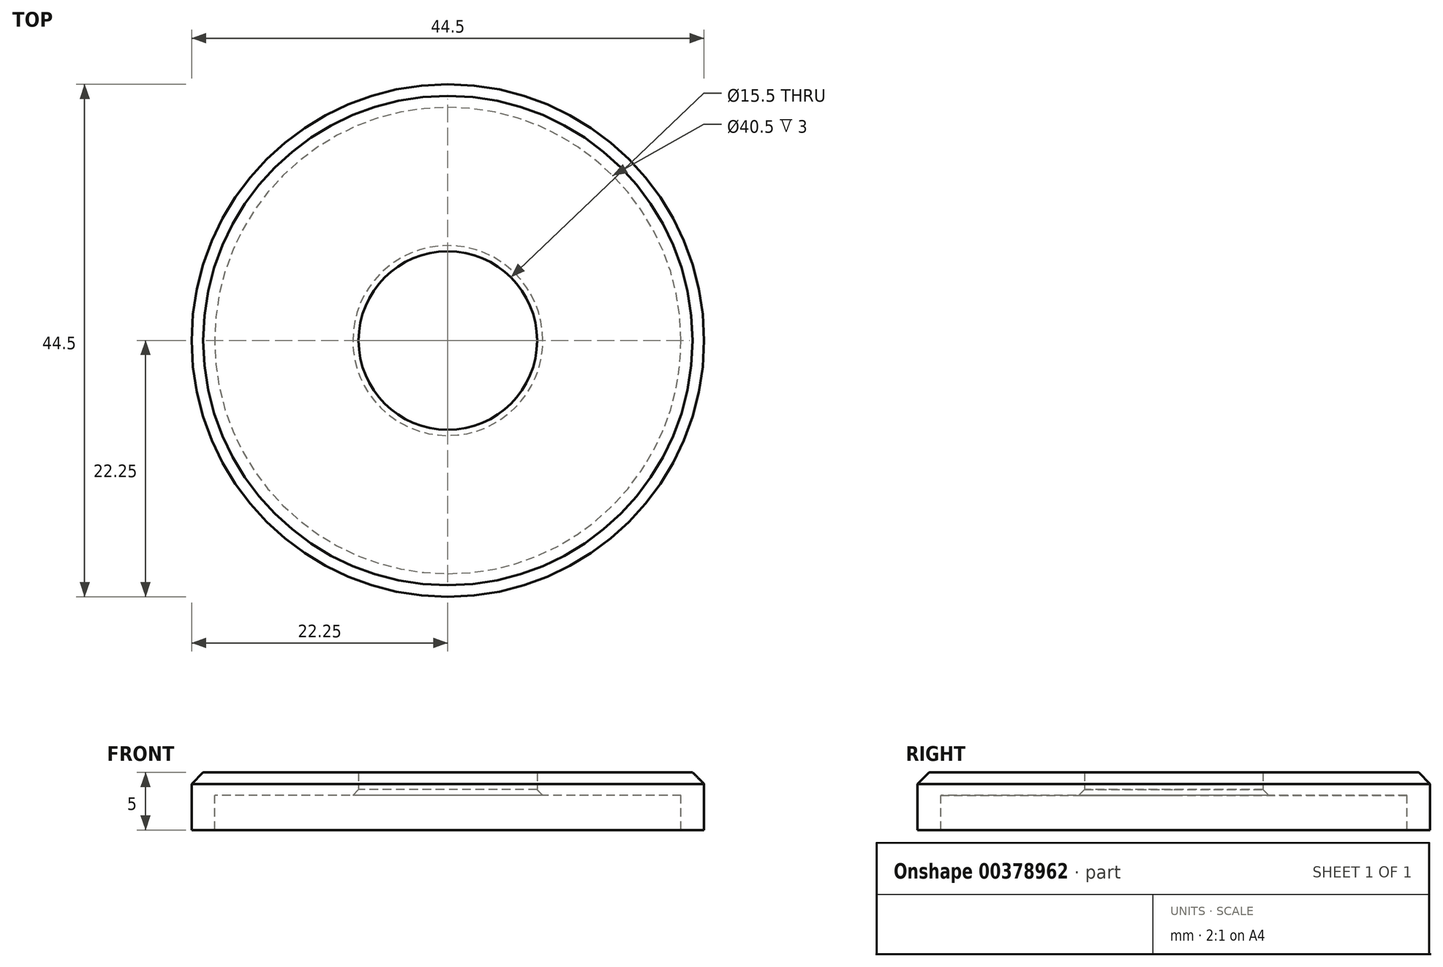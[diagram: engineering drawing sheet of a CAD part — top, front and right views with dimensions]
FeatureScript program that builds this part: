
annotation { "Feature Type Name" : "Feature", "Feature Type Description" : "" }
export const myFeature = defineFeature(function(context is Context, id is Id, definition is map)
    precondition{}
    {
        {
            var Q0;
            Q0=qCreatedBy(makeId("Top.planeOp"),FACE);
            var sketch = newSketch(context, id + "F0", { "sketchPlane" : qUnion([Q0])});
            skCircle(sketch, "E0", {"center": v(0, 0) * mm, "radius": 7.75 * mm});
            skCircle(sketch, "E1", {"center": v(0, 0) * mm, "radius": 20.25 * mm});
            skSolve(sketch);
        }
        {
            var Q0;
            Q0 = qSketchRegion(id + "F0", true);
            extrude(context, id + "F1", {"entities" : qUnion([Q0]), "depth" : 2 * mm});
        }
        {
            var Q0;
            Q0=makeQuery(id+"F1.opExtrude","CAP_FACE",FACE,{"disambiguationData":[OSD([sQuery(id+"F0.wireOp",EDGE,"E0"),sQuery(id+"F0.wireOp",EDGE,"E1")])],"isStart":false});
            var sketch = newSketch(context, id + "F2", { "sketchPlane" : qUnion([Q0])});
            skCircle(sketch, "E2.0", {"center": v(0, 0) * mm, "radius": 20.25 * mm});
            skCircle(sketch, "E3", {"center": v(0, 0) * mm, "radius": 22.25 * mm});
            skSolve(sketch);
        }
        {
            var Q0;
            Q0 = qSketchRegion(id + "F2", true);
            extrude(context, id + "F3", {"entities" : qUnion([Q0]), "operationType" : NewBodyOperationType.ADD, "oppositeDirection" : true, "depth" : 5 * mm});
        }
        {
            var Q0;
            Q0=makeQuery(id+"F1.opExtrude","CAP_EDGE",EDGE,{"disambiguationData":[OSD([sQuery(id+"F0.wireOp",EDGE,"E0")])],"isStart":true});
            chamfer(context, id + "F4", {"entities" : qUnion([Q0]), "width" : .5 * mm, "tangentPropagation" : true});
        }
        {
            var Q0;
            Q0=makeQuery(id+"F3.opExtrude","CAP_EDGE",EDGE,{"disambiguationData":[OSD([sQuery(id+"F2.wireOp",EDGE,"E3")])],"isStart":true});
            chamfer(context, id + "F5", {"entities" : qUnion([Q0]), "width" : 1 * mm, "tangentPropagation" : true});
        }
    });
